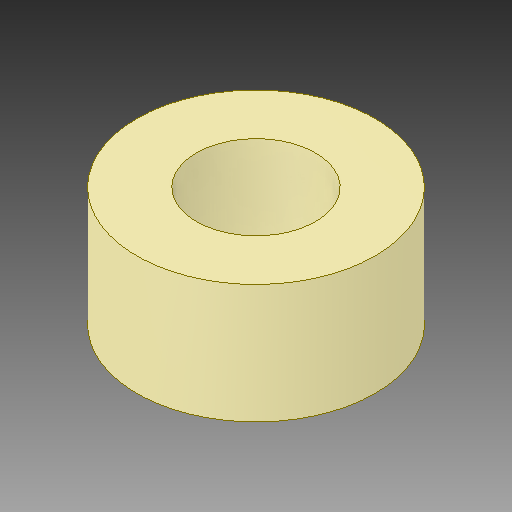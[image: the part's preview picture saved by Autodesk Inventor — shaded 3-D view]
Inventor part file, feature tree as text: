
AUTODESK INVENTOR PART (.ipt)
format: ipt  version: 2019 (Build 230136000, 136)  size: 95,744 bytes
history: native  units: in
note: dims shown in document units (in); Inventor stores cm internally (conversion verified against a paired STEP export)
features: extrude x1, sketch x1
ambient origin geometry x8: Origin, YZ Plane, XZ Plane, XY Plane, X Axis, Y Axis, Z Axis, Center Point
bodies: Solid1 (feature_tree)
feature tree (2):
  extrude  "Extrusion1"  Depth=0.25in
  sketch  "Sketch1"  dims[d0=0.5in d1=0.25in d2=0.25in d3=0.0in]
